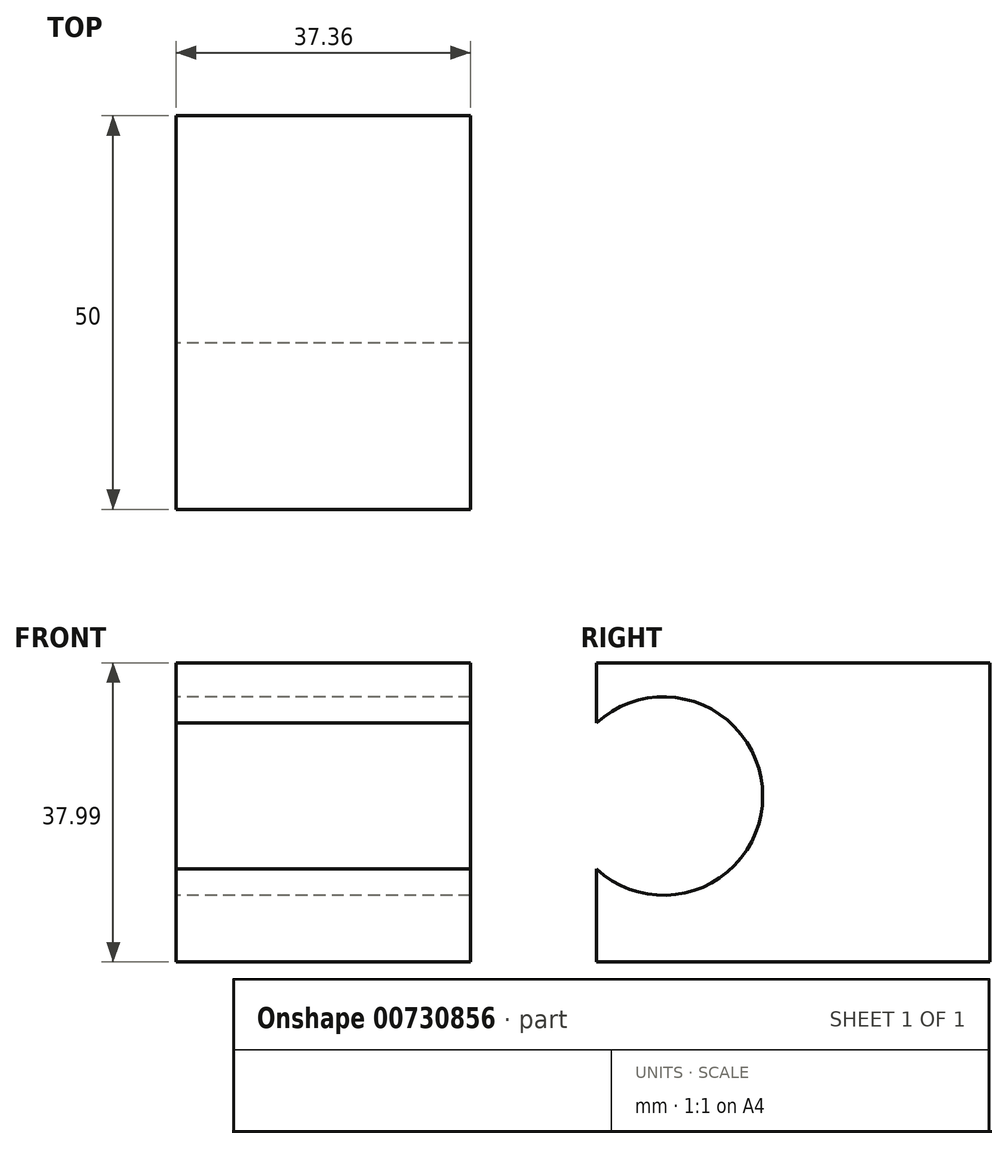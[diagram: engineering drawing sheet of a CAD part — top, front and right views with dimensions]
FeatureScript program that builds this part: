
annotation { "Feature Type Name" : "Feature", "Feature Type Description" : "" }
export const myFeature = defineFeature(function(context is Context, id is Id, definition is map)
    precondition{}
    {
        {
            var Q0;
            Q0=qCreatedBy(makeId("Front.planeOp"),FACE);
            var sketch = newSketch(context, id + "F0", { "sketchPlane" : qUnion([Q0])});
            skLineSegment(sketch, "E0.bottom", {"start": v(-30.65, 21.83) * mm, "end": v(6.71, 21.83) * mm});
            skLineSegment(sketch, "E0.top", {"start": v(-30.65, -16.16) * mm, "end": v(6.71, -16.16) * mm});
            skLineSegment(sketch, "E0.left", {"start": v(-30.65, 21.83) * mm, "end": v(-30.65, -16.16) * mm});
            skLineSegment(sketch, "E0.right", {"start": v(6.71, 21.83) * mm, "end": v(6.71, -16.16) * mm});
            skSolve(sketch);
        }
        {
            var Q0;
            Q0=makeQuery(id+"F0.imprint","IMPRINT",FACE,{"disambiguationData":[TD([[makeQuery(id+"F0.imprint","IMPRINT",EDGE,{"derivedFrom":sQuery(id+"F0.wireOp",EDGE,"E0.bottom")}),-1.0]])]});
            extrude(context, id + "F1", {"entities" : qUnion([Q0]), "endBound" : BoundingType.SYMMETRIC, "depth" : 50 * mm, "offsetDistance" : 25 * mm});
        }
        {
            var Q0;
            Q0=makeQuery(id+"F1.opExtrude","SWEPT_FACE",FACE,{"disambiguationData":[OSD([sQuery(id+"F0.wireOp",EDGE,"E0.left")])]});
            var sketch = newSketch(context, id + "F2", { "sketchPlane" : qUnion([Q0])});
            skCircle(sketch, "E1", {"center": v(16.47, 4.9) * mm, "radius": 12.6 * mm});
            skSolve(sketch);
        }
        {
            var Q0;
            Q0=makeQuery(id+"F2.imprint","IMPRINT",FACE,{"disambiguationData":[TD([[makeQuery(id+"F2.imprint","IMPRINT",EDGE,{"derivedFrom":sQuery(id+"F2.wireOp",EDGE,"E1")}),1.0]])]});
            var Q1;
            Q1=makeQuery(id+"F1.opExtrude","SWEPT_FACE",FACE,{"disambiguationData":[OSD([sQuery(id+"F0.wireOp",EDGE,"E0.right")])]});
            extrude(context, id + "F3", {"entities" : qUnion([Q0]), "operationType" : NewBodyOperationType.REMOVE, "endBound" : BoundingType.UP_TO_SURFACE, "oppositeDirection" : true, "depth" : 25 * mm, "endBoundEntityFace" : qUnion([Q1]), "offsetDistance" : 25 * mm});
        }
    });
